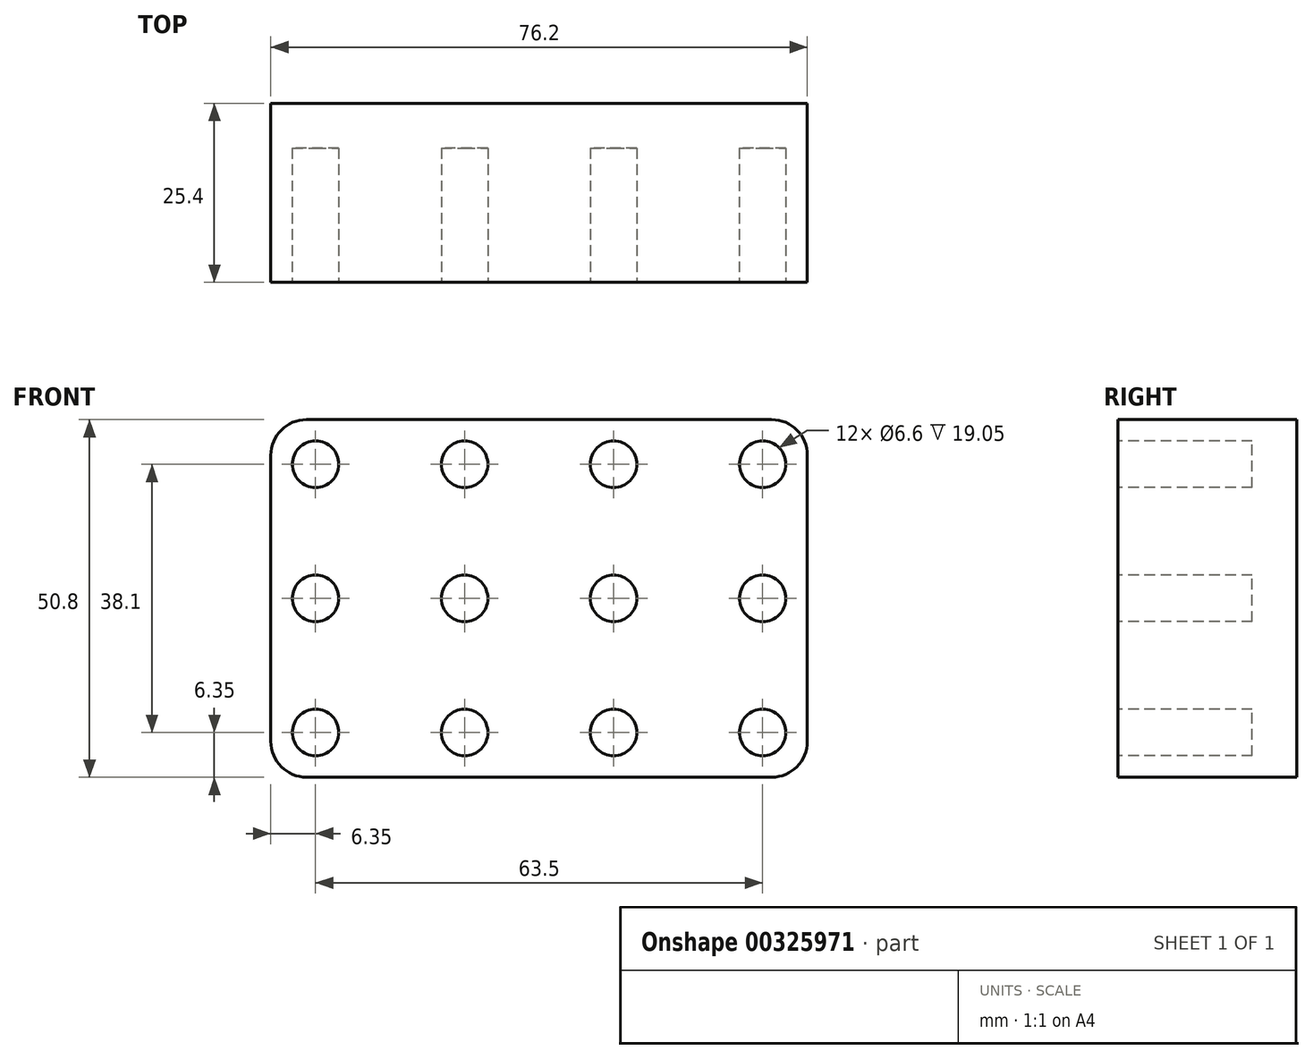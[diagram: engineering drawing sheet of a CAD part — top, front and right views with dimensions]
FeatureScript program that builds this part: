
annotation { "Feature Type Name" : "Feature", "Feature Type Description" : "" }
export const myFeature = defineFeature(function(context is Context, id is Id, definition is map)
    precondition{}
    {
        {
            var Q0;
            Q0=qCreatedBy(makeId("Front.planeOp"),FACE);
            var sketch = newSketch(context, id + "F0", { "sketchPlane" : qUnion([Q0])});
            skLineSegment(sketch, "E0.bottom", {"start": v(0, 0) * mm, "end": v(76.2, 0) * mm});
            skLineSegment(sketch, "E0.top", {"start": v(0, 50.8) * mm, "end": v(76.2, 50.8) * mm});
            skLineSegment(sketch, "E0.left", {"start": v(0, 0) * mm, "end": v(0, 50.8) * mm});
            skLineSegment(sketch, "E0.right", {"start": v(76.2, 0) * mm, "end": v(76.2, 50.8) * mm});
            skSolve(sketch);
        }
        {
            var Q0;
            Q0 = qSketchRegion(id + "F0", true);
            extrude(context, id + "F1", {"entities" : qUnion([Q0]), "depth" : 25.4 * mm});
        }
        {
            var Q0;
            Q0=makeQuery(id+"F1.opExtrude","CAP_FACE",FACE,{"disambiguationData":[OSD([sQuery(id+"F0.wireOp",EDGE,"E0.bottom"),sQuery(id+"F0.wireOp",EDGE,"E0.top"),sQuery(id+"F0.wireOp",EDGE,"E0.left"),sQuery(id+"F0.wireOp",EDGE,"E0.right")])],"isStart":false});
            var sketch = newSketch(context, id + "F2", { "sketchPlane" : qUnion([Q0])});
            skLineSegment(sketch, "E1.0", {"start": v(69.85, 44.45) * mm, "end": v(6.35, 44.45) * mm, "construction": true});
            skLineSegment(sketch, "E1.1", {"start": v(69.85, 6.35) * mm, "end": v(69.85, 44.45) * mm, "construction": true});
            skLineSegment(sketch, "E1.2", {"start": v(6.35, 6.35) * mm, "end": v(69.85, 6.35) * mm, "construction": true});
            skLineSegment(sketch, "E1.3", {"start": v(6.35, 44.45) * mm, "end": v(6.35, 6.35) * mm, "construction": true});
            skCircle(sketch, "E2", {"center": v(69.85, 6.35) * mm, "radius": 3.3 * mm});
            skCircle(sketch, "E3.0.1.0", {"center": v(69.85, 25.4) * mm, "radius": 3.3 * mm});
            skCircle(sketch, "E3.0.2.0", {"center": v(69.85, 44.45) * mm, "radius": 3.3 * mm});
            skCircle(sketch, "E3.1.0.0", {"center": v(48.68, 6.35) * mm, "radius": 3.3 * mm});
            skCircle(sketch, "E3.1.1.0", {"center": v(48.68, 25.4) * mm, "radius": 3.3 * mm});
            skCircle(sketch, "E3.1.2.0", {"center": v(48.68, 44.45) * mm, "radius": 3.3 * mm});
            skCircle(sketch, "E3.2.0.0", {"center": v(27.52, 6.35) * mm, "radius": 3.3 * mm});
            skCircle(sketch, "E3.2.1.0", {"center": v(27.52, 25.4) * mm, "radius": 3.3 * mm});
            skCircle(sketch, "E3.2.2.0", {"center": v(27.52, 44.45) * mm, "radius": 3.3 * mm});
            skCircle(sketch, "E3.3.0.0", {"center": v(6.35, 6.35) * mm, "radius": 3.3 * mm});
            skCircle(sketch, "E3.3.1.0", {"center": v(6.35, 25.4) * mm, "radius": 3.3 * mm});
            skCircle(sketch, "E3.3.2.0", {"center": v(6.35, 44.45) * mm, "radius": 3.3 * mm});
            skLineSegment(sketch, "E3.direction1", {"start": v(69.85, 6.35) * mm, "end": v(48.68, 6.35) * mm, "construction": true});
            skLineSegment(sketch, "E3.direction2", {"start": v(69.85, 6.35) * mm, "end": v(69.85, 25.4) * mm, "construction": true});
            skSolve(sketch);
        }
        {
            var Q0;
            Q0 = qSketchRegion(id + "F2", true);
            extrude(context, id + "F3", {"entities" : qUnion([Q0]), "operationType" : NewBodyOperationType.REMOVE, "oppositeDirection" : true, "depth" : 19.05 * mm});
        }
        {
            var Q0;
            Q0=makeQuery(id+"F1.opExtrude","SWEPT_EDGE",EDGE,{"disambiguationData":[OSD([sQuery(id+"F0.wireOp",EDGE,"E0.top"),sQuery(id+"F0.wireOp",EDGE,"E0.right")])]});
            var Q1;
            Q1=makeQuery(id+"F1.opExtrude","SWEPT_EDGE",EDGE,{"disambiguationData":[OSD([sQuery(id+"F0.wireOp",EDGE,"E0.top"),sQuery(id+"F0.wireOp",EDGE,"E0.left")])]});
            var Q2;
            Q2=makeQuery(id+"F1.opExtrude","SWEPT_EDGE",EDGE,{"disambiguationData":[OSD([sQuery(id+"F0.wireOp",EDGE,"E0.bottom"),sQuery(id+"F0.wireOp",EDGE,"E0.left")])]});
            var Q3;
            Q3=makeQuery(id+"F1.opExtrude","SWEPT_EDGE",EDGE,{"disambiguationData":[OSD([sQuery(id+"F0.wireOp",EDGE,"E0.bottom"),sQuery(id+"F0.wireOp",EDGE,"E0.right")])]});
            fillet(context, id + "F4", {"entities" : qUnion([Q0, Q1, Q2, Q3]), "radius" : 5.08 * mm, "tangentPropagation" : true, "allowEdgeOverflow" : false});
        }
    });
